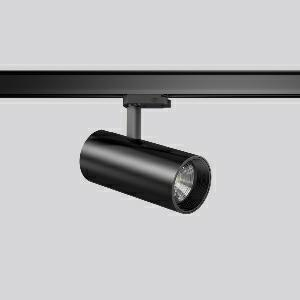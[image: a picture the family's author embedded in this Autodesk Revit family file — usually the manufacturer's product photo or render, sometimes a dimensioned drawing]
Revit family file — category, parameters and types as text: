
# Revit family: deecos_s_mini_742194_003_1_8cfb
name_source: partatom
category: Lighting Fixtures
units: mm (PartAtom-declared; Revit-internal decimal feet)

## family parameters
Cut with Voids When Loaded = No
Host = Face
Light Source = No
Part Type = Normal
Room Calculation Point = No
Round Connector Dimension = Use Diameter
Shared = No

## types (1)
- DEECOS S mini (1 x LED Modul 940, 2250 lm, 4000)
    Apparent Load = 22 VA
    Approval mark = CE
    CIE Flux Codes = 99 100 100 100 100
    Color Rendering = 92
    Color Temperature = 4000
    Default Elevation = 1800 mm
    Description = Series: DEECOS S mini
LED surface-mounted projector in modern design with no visible cooling ribs. Housing: die-cast aluminium, powder-coated. Rotation range: 356°. Swivel range: 90°. Black plastic ring and recessed LED to prevent glare from the side. Optical assembly with lens made of plastic (polycarbonate) for the best homogeneous light distribution - can be changed without tools. Best colour rendering index Ra>90. Superspot version with small spot LED. With multi adaptor for 3-circuit tracks 230 V. Suitable for Track on ceiling, Wall track. High quality converter without flickering and stroboscopic effect. The following accessories can be mounted without use of tools: interchangeable lenses, decorative glasses, honeycomb louvre, clear and frosted diffusers, white interchangeable plastic ring. 
Colour: deep black, matt (RAL 9005)
Diameter: 87 mm
Height: 214 mm
Lamp: LED
Socket: without socket
Colour temperature: 4000K
Colour rendering index (CRI): 92
System power: 22 W
Rated luminous flux: 2250 lm
Luminous efficiency: 102 lm/W
Control gear: Regulated power supply
Protection class: I
Type of protection: IP 20
    Height = 214 mm
    Lamp = 1 x LED Modul 940
    Lamp Light Flux = 2250 lm
    Lamp count = 1
    Length = 87 mm
    Lifetime = 50000 h
    Luminous efficacy = 102 lm/W
    Manufacturer = RZB
    ModVariant = No
    Model = 742194.003.1
    Mounting Place = Ceiling
    Mounting Type = Rail mounted
    Number of Poles = 1
    OnlyDefault = Yes
    Power Factor = 1
    Product Name = DEECOS S mini
    Product group = Track mounted projectors
    ProductGroupID = 301
    Protection Class = Protection class I
    Protection Degree = IP 20
    RLX_Detail_Level = 1
    RLX_Emergency_Light_Flux = 0 lm
    RLX_Emergency_Type = 0
    RLX_Emergency_Type_DB = No
    RlxData = <blob elided: 38797 chars, md5=fe2b8ed0>
    Socket = socket
    Standby Power = 0 W
    System Light Flux = 2250 lm
    System Power = 22 W
    Type Comments = Product without accessories
    Type Image = 741930.003.jpg
    URL = http://relux.com
    VarID = ---
    Voltage = 230 V
    Voltage Range = 220-240 V
    Weight = 0.00 kg
    Width = 0 mm  [stored 0 ft]

note: [stored X ft] marks values corroborated as IEEE doubles in the binary element streams (Revit-internal decimal feet)

## geometry (parser evidence)
native form markers: Blend x4, Sweep x10
no freeform markers — native parametric forms only
